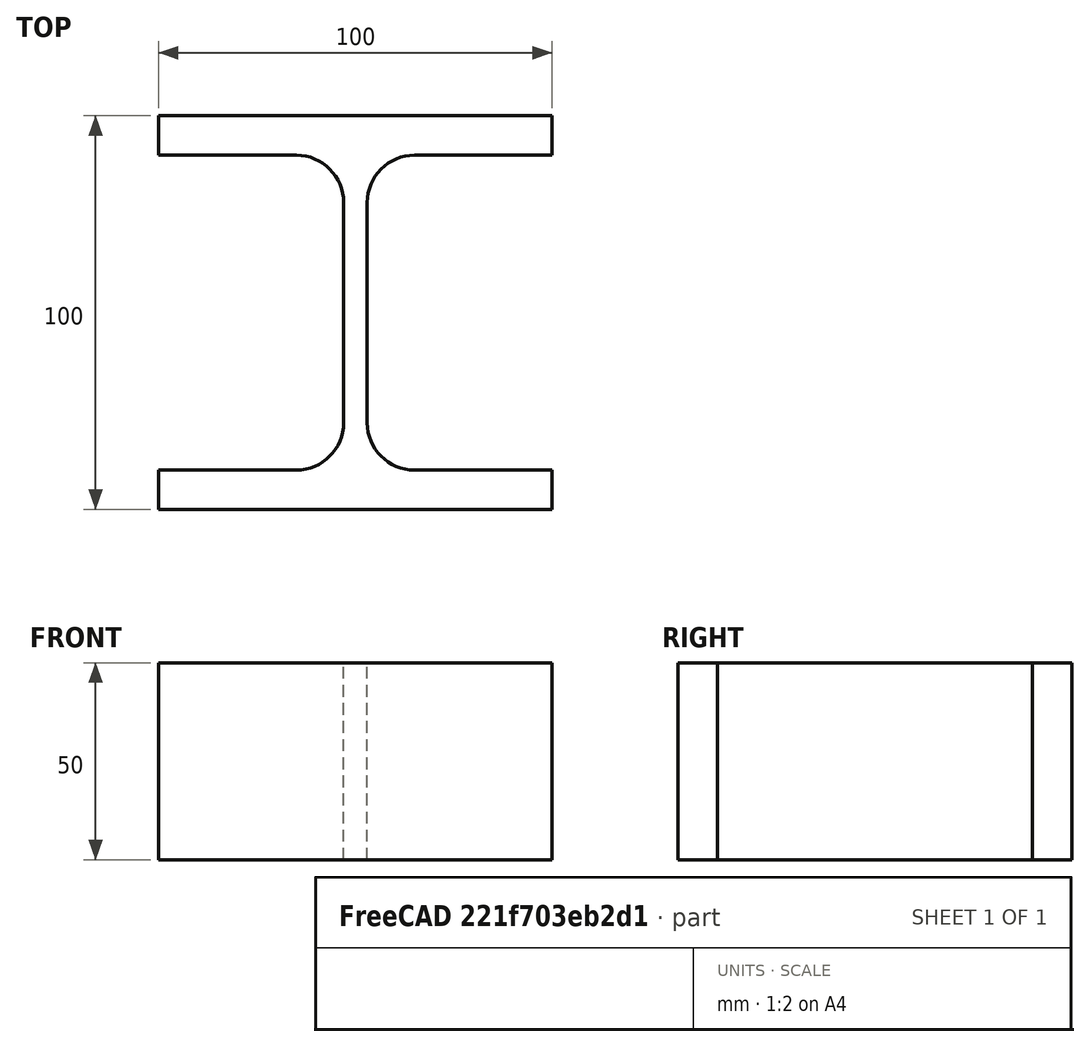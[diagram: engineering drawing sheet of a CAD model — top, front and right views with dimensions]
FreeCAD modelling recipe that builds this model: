
FCSTD DOCUMENT  (FreeCAD 0.15R4671 (Git))
Label: HE-B-Profile 100 DIN1025-2 S235JR
License: All rights reserved
LicenseURL: http://en.wikipedia.org/wiki/All_rights_reserved
objects: Sketcher::SketchObject×1, Part::Extrusion×1
note: 2 computed .brp shape members not serialized (recipe doc carries the construction recipe); baked Part::Feature solids carry a one-line shape summary decoded from their .brp

FEATURE [Sketcher::SketchObject] Sketch
  sketch-geometry (16):
    g0: LineSegment StartX=3 StartY=-28 StartZ=0 EndX=3 EndY=28 EndZ=0
    g1: LineSegment StartX=15 StartY=40 StartZ=0 EndX=50 EndY=40 EndZ=0
    g2: LineSegment StartX=50 StartY=40 StartZ=0 EndX=50 EndY=50 EndZ=0
    g3: LineSegment StartX=50 StartY=50 StartZ=0 EndX=-50 EndY=50 EndZ=0
    g4: LineSegment StartX=-50 StartY=50 StartZ=0 EndX=-50 EndY=40 EndZ=0
    g5: LineSegment StartX=-50 StartY=40 StartZ=0 EndX=-15 EndY=40 EndZ=0
    g6: LineSegment StartX=-3 StartY=28 StartZ=0 EndX=-3 EndY=-28 EndZ=0
    g7: LineSegment StartX=-15 StartY=-40 StartZ=0 EndX=-50 EndY=-40 EndZ=0
    g8: LineSegment StartX=-50 StartY=-40 StartZ=0 EndX=-50 EndY=-50 EndZ=0
    g9: LineSegment StartX=-50 StartY=-50 StartZ=0 EndX=50 EndY=-50 EndZ=0
    g10: LineSegment StartX=50 StartY=-50 StartZ=0 EndX=50 EndY=-40 EndZ=0
    g11: LineSegment StartX=50 StartY=-40 StartZ=0 EndX=15 EndY=-40 EndZ=0
    g12: ArcOfCircle CenterX=15 CenterY=28 CenterZ=0 NormalX=0 NormalY=0 NormalZ=1 Radius=12 StartAngle=1.5708 EndAngle=3.14159
    g13: ArcOfCircle CenterX=15 CenterY=-28 CenterZ=0 NormalX=0 NormalY=0 NormalZ=1 Radius=12 StartAngle=3.14159 EndAngle=4.71239
    g14: ArcOfCircle CenterX=-15 CenterY=28 CenterZ=0 NormalX=0 NormalY=0 NormalZ=1 Radius=12 StartAngle=0 EndAngle=1.5708
    g15: ArcOfCircle CenterX=-15 CenterY=-28 CenterZ=0 NormalX=0 NormalY=0 NormalZ=1 Radius=12 StartAngle=4.71239 EndAngle=6.28319
  constraints (42):
    c: Vertical(g0)
    c: Coincident(g2,g1)
    c: Vertical(g2)
    c: Coincident(g3,g2)
    c: Coincident(g4,g3)
    c: Vertical(g4)
    c: Coincident(g5,g4)
    c: Horizontal(g5)
    c: Vertical(g6)
    c: Horizontal(g7)
    c: Coincident(g8,g7)
    c: Vertical(g8)
    c: Coincident(g9,g8)
    c: Horizontal(g9)
    c: Coincident(g10,g9)
    c: Vertical(g10)
    c: Coincident(g11,g10)
    c: Horizontal(g11)
    c: Tangent(g1,g12) = 1.5708
    c: Tangent(g0,g12) = 1.5708
    c: Tangent(g0,g13) = 1.5708
    c: Tangent(g11,g13) = 1.5708
    c: Tangent(g5,g14) = 1.5708
    c: Tangent(g6,g14) = 1.5708
    c: Tangent(g6,g15) = 1.5708
    c: Tangent(g7,g15) = 1.5708
    c: Equal(g3,g9)
    c: Equal(g2,g4)
    c: Equal(g4,g8)
    c: Equal(g8,g10)
    c: Equal(g12,g14)
    c: Equal(g14,g15)
    c: Equal(g15,g13)
    c: Symmetric(g2,g3,g-2)
    c: Symmetric(g9,g8,g-2)
    c: Symmetric(g0,g6,g-2)
    c: Symmetric(g2,g9,g-1)
    c: DistanceY(g2,g9) = -100
    c: DistanceX(g3) = -100
    c: DistanceX(g0,g6) = -6
    c: DistanceY(g2) = 10
    c: Radius(g12) = 12
FEATURE [Part::Extrusion] Extrude  label="HE-B-Profile 100 DIN1025-2 S235JR"
  Base = -> Sketch
  Dir = (0,0,50)
  Solid = true
